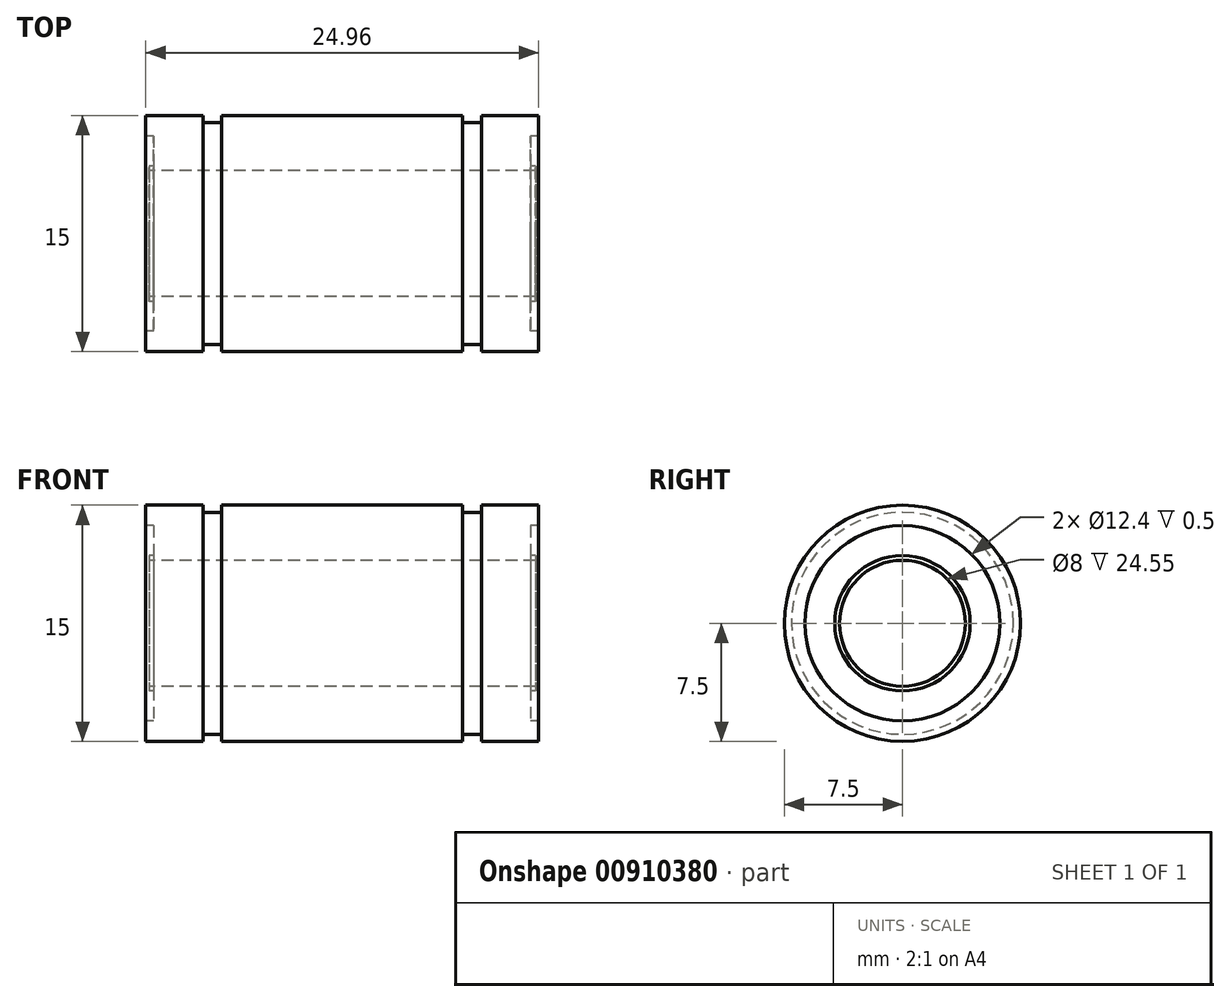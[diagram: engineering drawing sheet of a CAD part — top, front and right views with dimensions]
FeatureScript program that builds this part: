
annotation { "Feature Type Name" : "Feature", "Feature Type Description" : "" }
export const myFeature = defineFeature(function(context is Context, id is Id, definition is map)
    precondition{}
    {
        {
            var Q0;
            Q0=qCreatedBy(makeId("Front.planeOp"),FACE);
            var sketch = newSketch(context, id + "F0", { "sketchPlane" : qUnion([Q0])});
            skLineSegment(sketch, "E0.bottom", {"start": v(12.47, 7.5) * mm, "end": v(8.85, 7.5) * mm});
            skLineSegment(sketch, "E0.top", {"start": v(12.27, 4) * mm, "end": v(-12.27, 4) * mm});
            skLineSegment(sketch, "E0.left", {"start": v(12.47, 7.5) * mm, "end": v(12.47, 6.2) * mm});
            skLineSegment(sketch, "E0.right", {"start": v(-12.47, 7.5) * mm, "end": v(-12.47, 6.2) * mm});
            skPoint(sketch, "E0.middle", {"position": v(0, 5.75) * mm});
            skLineSegment(sketch, "E1", {"start": v(-8.85, 7.5) * mm, "end": v(-8.85, 7.05) * mm});
            skLineSegment(sketch, "E2", {"start": v(-8.85, 7.05) * mm, "end": v(-7.65, 7.05) * mm});
            skLineSegment(sketch, "E3", {"start": v(-7.65, 7.05) * mm, "end": v(-7.65, 7.5) * mm});
            skLineSegment(sketch, "E4", {"start": v(7.65, 7.5) * mm, "end": v(7.65, 7.05) * mm});
            skLineSegment(sketch, "E5", {"start": v(7.65, 7.05) * mm, "end": v(8.85, 7.05) * mm});
            skLineSegment(sketch, "E6", {"start": v(8.85, 7.05) * mm, "end": v(8.85, 7.5) * mm});
            skLineSegment(sketch, "E7.trimOffspring", {"start": v(-8.85, 7.5) * mm, "end": v(-12.47, 7.5) * mm});
            skLineSegment(sketch, "E8.trimOffspring", {"start": v(7.65, 7.5) * mm, "end": v(-7.65, 7.5) * mm});
            skLineSegment(sketch, "E9", {"start": v(0, 0) * mm, "end": v(6.6, 0) * mm, "construction": true});
            skLineSegment(sketch, "E10", {"start": v(12.47, 6.2) * mm, "end": v(11.97, 6.2) * mm});
            skLineSegment(sketch, "E11", {"start": v(11.97, 6.2) * mm, "end": v(11.97, 4.3) * mm});
            skLineSegment(sketch, "E12", {"start": v(-12.47, 6.2) * mm, "end": v(-11.97, 6.2) * mm});
            skLineSegment(sketch, "E13", {"start": v(-11.97, 6.2) * mm, "end": v(-11.97, 4.3) * mm});
            skPoint(sketch, "E14.orphan", {"position": v(-12.47, 4) * mm});
            skPoint(sketch, "E15.orphan", {"position": v(12.47, 4) * mm});
            skLineSegment(sketch, "E16", {"start": v(-11.97, 4.3) * mm, "end": v(-12.27, 4.3) * mm});
            skLineSegment(sketch, "E17", {"start": v(-12.27, 4.3) * mm, "end": v(-12.27, 4) * mm});
            skLineSegment(sketch, "E18", {"start": v(11.97, 4.3) * mm, "end": v(12.27, 4.3) * mm});
            skLineSegment(sketch, "E19", {"start": v(12.27, 4.3) * mm, "end": v(12.27, 4) * mm});
            skSolve(sketch);
        }
        {
            var Q0;
            Q0 = qSketchRegion(id + "F0", true);
            var Q1;
            Q1=sQuery(id+"F0.wireOp",EDGE,"E9");
            revolve(context, id + "F1", {"surfaceOperationType" : NewSurfaceOperationType.NEW, "entities" : qUnion([Q0]), "axis" : qUnion([Q1]), "revolveType" : RevolveType.FULL});
        }
    });
